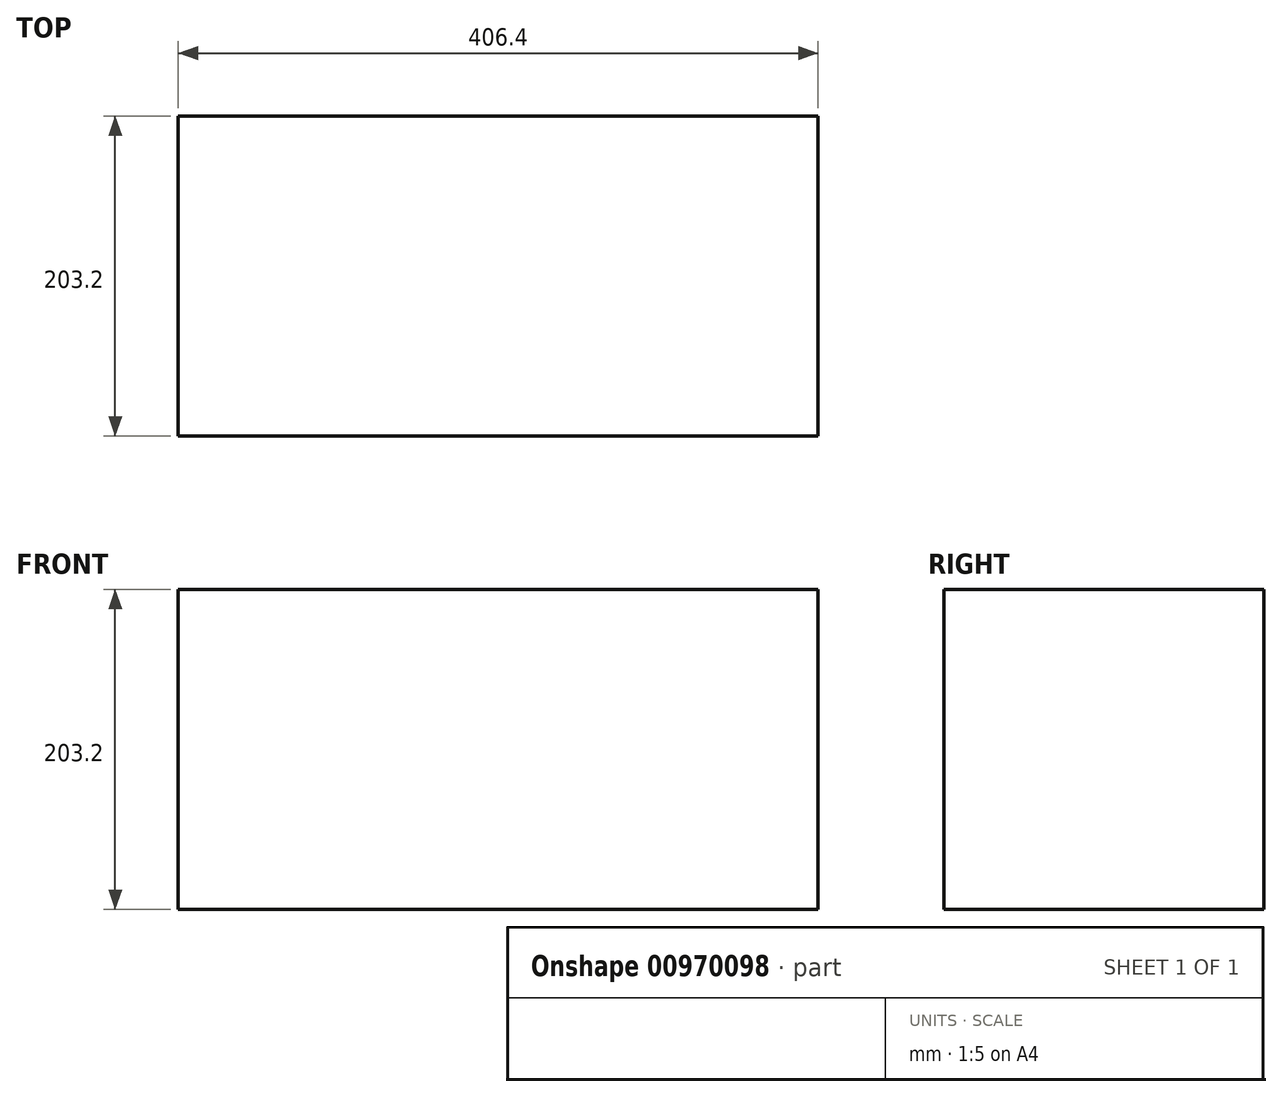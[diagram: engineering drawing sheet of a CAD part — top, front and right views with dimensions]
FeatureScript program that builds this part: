
annotation { "Feature Type Name" : "Feature", "Feature Type Description" : "" }
export const myFeature = defineFeature(function(context is Context, id is Id, definition is map)
    precondition{}
    {
        {
            var Q0;
            Q0=qCreatedBy(makeId("Top.planeOp"),FACE);
            var sketch = newSketch(context, id + "F0", { "sketchPlane" : qUnion([Q0])});
            skLineSegment(sketch, "E0.bottom", {"start": v(-137.34, 88.85) * mm, "end": v(269.06, 88.85) * mm});
            skLineSegment(sketch, "E0.top", {"start": v(-137.34, -114.35) * mm, "end": v(269.06, -114.35) * mm});
            skLineSegment(sketch, "E0.left", {"start": v(-137.34, 88.85) * mm, "end": v(-137.34, -114.35) * mm});
            skLineSegment(sketch, "E0.right", {"start": v(269.06, 88.85) * mm, "end": v(269.06, -114.35) * mm});
            skSolve(sketch);
        }
        {
            var Q0;
            Q0=makeQuery(id+"F0.imprint","IMPRINT",FACE,{"disambiguationData":[TD([[makeQuery(id+"F0.imprint","IMPRINT",EDGE,{"derivedFrom":sQuery(id+"F0.wireOp",EDGE,"E0.bottom")}),-1.0]])]});
            extrude(context, id + "F1", {"entities" : qUnion([Q0]), "depth" : 203.2 * mm, "offsetDistance" : 25.4 * mm});
        }
    });
